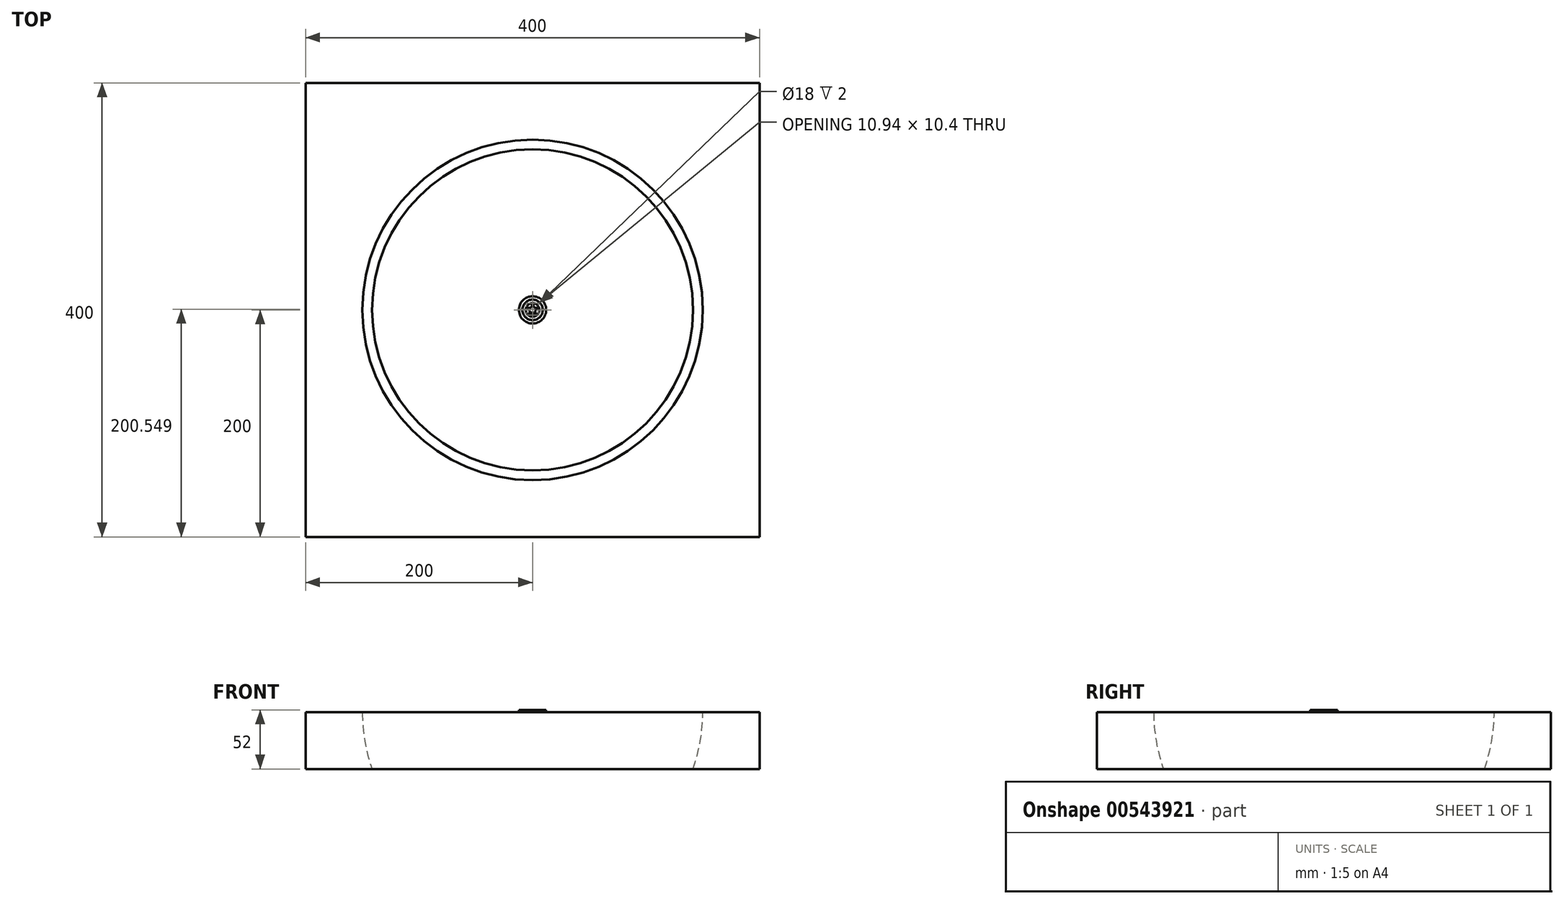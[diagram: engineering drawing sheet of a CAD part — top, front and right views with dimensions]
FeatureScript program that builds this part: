
annotation { "Feature Type Name" : "Feature", "Feature Type Description" : "" }
export const myFeature = defineFeature(function(context is Context, id is Id, definition is map)
    precondition{}
    {
        {
            var Q0;
            Q0=qCreatedBy(makeId("Top.planeOp"),FACE);
            var sketch = newSketch(context, id + "F0", { "sketchPlane" : qUnion([Q0])});
            skLineSegment(sketch, "E0.bottom", {"start": v(200, 200) * mm, "end": v(-200, 200) * mm});
            skLineSegment(sketch, "E0.top", {"start": v(200, -200) * mm, "end": v(-200, -200) * mm});
            skLineSegment(sketch, "E0.left", {"start": v(200, 200) * mm, "end": v(200, -200) * mm});
            skLineSegment(sketch, "E0.right", {"start": v(-200, 200) * mm, "end": v(-200, -200) * mm});
            skPoint(sketch, "E0.middle", {"position": v(0, 0) * mm});
            skSolve(sketch);
        }
        {
            var Q0;
            Q0 = qSketchRegion(id + "F0", true);
            extrude(context, id + "F1", {"entities" : qUnion([Q0]), "depth" : 50 * mm, "offsetDistance" : 25 * mm});
        }
        {
            var Q0;
            Q0=makeQuery(id+"F1.opExtrude","CAP_FACE",FACE,{"disambiguationData":[OSD([sQuery(id+"F0.wireOp",EDGE,"E0.bottom"),sQuery(id+"F0.wireOp",EDGE,"E0.top"),sQuery(id+"F0.wireOp",EDGE,"E0.left"),sQuery(id+"F0.wireOp",EDGE,"E0.right")])],"isStart":false});
            var sketch = newSketch(context, id + "F2", { "sketchPlane" : qUnion([Q0])});
            skCircle(sketch, "E1", {"center": v(0, 0) * mm, "radius": 150 * mm});
            skLineSegment(sketch, "E2", {"start": v(0, 177.28) * mm, "end": v(0, -175.41) * mm});
            skSolve(sketch);
        }
        {
            var Q0;
            {var subQ0=sQuery(id+"F2.wireOp",EDGE,"E2");var subQ1=sQuery(id+"F2.wireOp",EDGE,"E1");var subQ2=makeQuery(id+"F2.imprint","INTERSECT",VERTEX,{"disambiguationData":[OD(0.0)],"derivedFrom":[subQ1,subQ0]});Q0=makeQuery(id+"F2.imprint","IMPRINT",FACE,{"disambiguationData":[TD([[makeQuery(id+"F2.imprint","IMPRINT",EDGE,{"disambiguationData":[TD([[subQ2,-1.0]])],"derivedFrom":subQ1}),1.0]])]});}
            var Q1;
            Q1=sQuery(id+"F2.wireOp",EDGE,"E2");
            revolve(context, id + "F3", {"operationType" : NewBodyOperationType.REMOVE, "entities" : qUnion([Q0]), "axis" : qUnion([Q1]), "revolveType" : RevolveType.FULL, "oppositeDirection" : true});
        }
        {
            var Q0;
            Q0=makeQuery(id+"F1.opExtrude","CAP_FACE",FACE,{"disambiguationData":[OSD([sQuery(id+"F0.wireOp",EDGE,"E0.bottom"),sQuery(id+"F0.wireOp",EDGE,"E0.top"),sQuery(id+"F0.wireOp",EDGE,"E0.left"),sQuery(id+"F0.wireOp",EDGE,"E0.right")])],"isStart":false});
            var sketch = newSketch(context, id + "F4", { "sketchPlane" : qUnion([Q0])});
            skCircle(sketch, "E3", {"center": v(0, 0) * mm, "radius": 6 * mm});
            skCircle(sketch, "E4", {"center": v(0, 0) * mm, "radius": 9 * mm});
            skCircle(sketch, "E5", {"center": v(0, 0) * mm, "radius": 12 * mm});
            skLineSegment(sketch, "E6.bottom", {"start": v(200, 200) * mm, "end": v(-200, 200) * mm});
            skLineSegment(sketch, "E6.top", {"start": v(200, -200) * mm, "end": v(-200, -200) * mm});
            skLineSegment(sketch, "E6.left", {"start": v(200, 200) * mm, "end": v(200, -200) * mm});
            skLineSegment(sketch, "E6.right", {"start": v(-200, 200) * mm, "end": v(-200, -200) * mm});
            skLineSegment(sketch, "E7.0.0", {"start": v(-200, -200) * mm, "end": v(200, -200) * mm});
            skLineSegment(sketch, "E7.0.1", {"start": v(200, -200) * mm, "end": v(200, 200) * mm});
            skCircle(sketch, "E8.cCircle", {"center": v(0, 0) * mm, "radius": 6 * mm, "construction": true});
            skLineSegment(sketch, "E9", {"start": v(-5.47, 1.78) * mm, "end": v(5.47, 1.78) * mm});
            skLineSegment(sketch, "E10", {"start": v(-3.38, -4.65) * mm, "end": v(5.47, 1.78) * mm});
            skLineSegment(sketch, "E11", {"start": v(0, 5.75) * mm, "end": v(-3.38, -4.65) * mm});
            skLineSegment(sketch, "E12", {"start": v(0, 5.75) * mm, "end": v(3.38, -4.65) * mm});
            skLineSegment(sketch, "E13", {"start": v(-5.47, 1.78) * mm, "end": v(3.38, -4.65) * mm});
            skSolve(sketch);
        }
        {
            var Q0;
            Q0=makeQuery(id+"F4.imprint","IMPRINT",FACE,{"disambiguationData":[TD([[makeQuery(id+"F4.imprint","IMPRINT",EDGE,{"derivedFrom":sQuery(id+"F4.wireOp",EDGE,"E4")}),-1.0]])]});
            extrude(context, id + "F5", {"entities" : qUnion([Q0]), "depth" : 2 * mm, "offsetDistance" : 25 * mm});
        }
        {
            var Q0;
            Q0=makeQuery(id+"F4.imprint","IMPRINT",FACE,{"disambiguationData":[TD([[makeQuery(id+"F4.imprint","IMPRINT",EDGE,{"derivedFrom":sQuery(id+"F4.wireOp",EDGE,"E3")}),1.0]])]});
            extrude(context, id + "F6", {"entities" : qUnion([Q0]), "depth" : 2 * mm, "offsetDistance" : 25 * mm});
        }
    });
